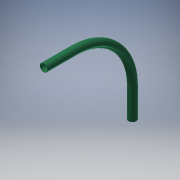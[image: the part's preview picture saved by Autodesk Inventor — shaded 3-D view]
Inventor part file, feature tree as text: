
AUTODESK INVENTOR PART (.ipt)
format: ipt  version: 2016 (Build 200138000, 138)  size: 152,576 bytes
history: native  units: in
note: dims shown in document units (in); Inventor stores cm internally (conversion verified against a paired STEP export)
features: sketch x4, extrude x2, plane x1, sweep x1
ambient origin geometry x8: Origin, YZ Plane, XZ Plane, XY Plane, X Axis, Y Axis, Z Axis, Center Point
bodies: Solid1 (feature_tree)
feature tree (8):
  extrude  "Extrusion1"  Depth=0.0591in
  sketch  "Sketch4"  dims[d2=6.0in d3=0.0in d7=12.0in]
  plane  "Work Plane4"
  sweep  "Sweep1"
  extrude  "Extrusion2"  Depth=6.0in TaperAngle=0.0deg
  sketch  "Sketch1"  dims[d0=1.5748in d1=0.0591in]
  sketch  "Sketch8"  dims[d9=0.0in d10=6.0in d11=0.0in]
  sketch  "Sketch9"  dims[d12=0.0in]
